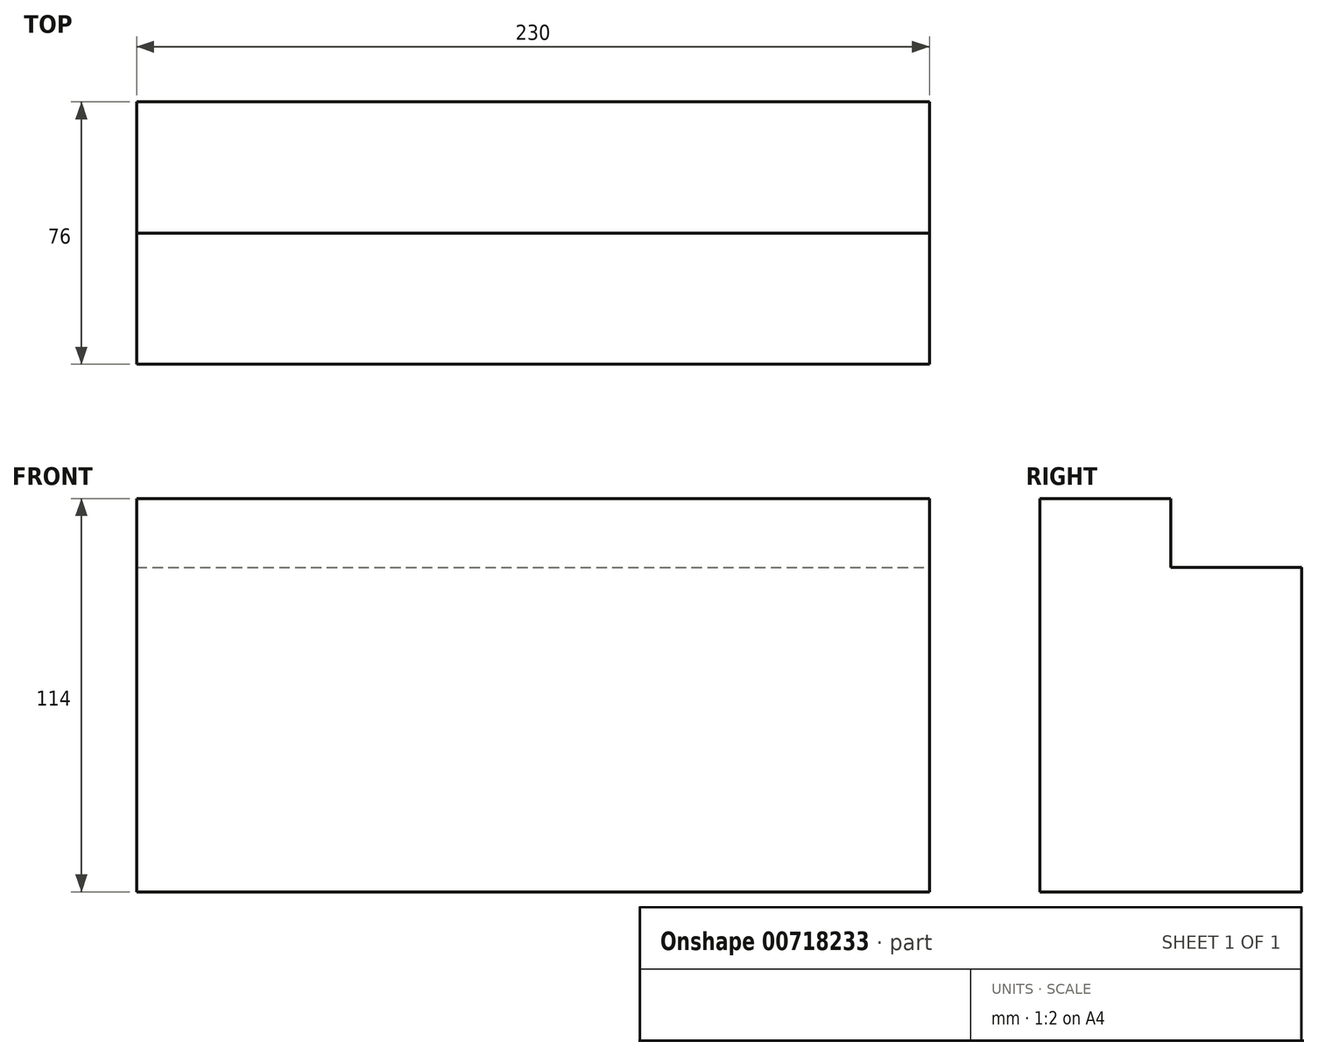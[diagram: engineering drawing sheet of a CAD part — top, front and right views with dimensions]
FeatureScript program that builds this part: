
annotation { "Feature Type Name" : "Feature", "Feature Type Description" : "" }
export const myFeature = defineFeature(function(context is Context, id is Id, definition is map)
    precondition{}
    {
        {
            var Q0;
            Q0=qCreatedBy(makeId("Front.planeOp"),FACE);
            var sketch = newSketch(context, id + "F0", { "sketchPlane" : qUnion([Q0])});
            skLineSegment(sketch, "E0.bottom", {"start": v(115, -57) * mm, "end": v(-115, -57) * mm});
            skLineSegment(sketch, "E0.top", {"start": v(115, 57) * mm, "end": v(-115, 57) * mm});
            skLineSegment(sketch, "E0.left", {"start": v(115, -57) * mm, "end": v(115, 57) * mm});
            skLineSegment(sketch, "E0.right", {"start": v(-115, -57) * mm, "end": v(-115, 57) * mm});
            skPoint(sketch, "E0.middle", {"position": v(0, 0) * mm});
            skSolve(sketch);
        }
        {
            var Q0;
            Q0=makeQuery(id+"F0.imprint","IMPRINT",FACE,{"disambiguationData":[TD([[makeQuery(id+"F0.imprint","IMPRINT",EDGE,{"derivedFrom":sQuery(id+"F0.wireOp",EDGE,"E0.bottom")}),-1.0]])]});
            extrude(context, id + "F1", {"entities" : qUnion([Q0]), "depth" : 76 * mm, "offsetDistance" : 25 * mm});
        }
        {
            var Q0;
            Q0=qCreatedBy(makeId("Right.planeOp"),FACE);
            cPlane(context, id + "F2", {"entities" : qUnion([Q0]), "cplaneType" : CPlaneType.OFFSET, "offset" : 115 * mm, "width" : 150 * mm, "height" : 150 * mm});
        }
        {
            var Q0;
            Q0=qCreatedBy(id+"F2.planeOp",FACE);
            var sketch = newSketch(context, id + "F3", { "sketchPlane" : qUnion([Q0])});
            skLineSegment(sketch, "E1.bottom", {"start": v(0, 57) * mm, "end": v(-38, 57) * mm});
            skLineSegment(sketch, "E1.top", {"start": v(0, 37) * mm, "end": v(-38, 37) * mm});
            skLineSegment(sketch, "E1.left", {"start": v(0, 57) * mm, "end": v(0, 37) * mm});
            skLineSegment(sketch, "E1.right", {"start": v(-38, 57) * mm, "end": v(-38, 37) * mm});
            skSolve(sketch);
        }
        {
            var Q0;
            Q0=makeQuery(id+"F3.imprint","IMPRINT",FACE,{"disambiguationData":[TD([[makeQuery(id+"F3.imprint","IMPRINT",EDGE,{"derivedFrom":sQuery(id+"F3.wireOp",EDGE,"E1.bottom")}),1.0]])]});
            extrude(context, id + "F4", {"entities" : qUnion([Q0]), "operationType" : NewBodyOperationType.REMOVE, "endBound" : BoundingType.THROUGH_ALL, "oppositeDirection" : true, "depth" : 25 * mm, "offsetDistance" : 25 * mm});
        }
    });
